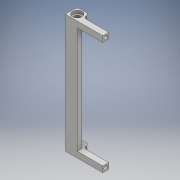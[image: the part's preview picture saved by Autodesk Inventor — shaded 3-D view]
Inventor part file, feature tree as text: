
AUTODESK INVENTOR PART (.ipt)
format: ipt  version: 2018 (Build 220112000, 112)  size: 217,088 bytes
history: native  units: mm
features: extrude x11, sketch x11, fillet x3
ambient origin geometry x8: Origin, YZ Plane, XZ Plane, XY Plane, X Axis, Y Axis, Z Axis, Center Point
bodies: Solid1 (feature_tree)
feature tree (25):
  extrude  "Extrusion1"  Depth=200.0mm
  extrude  "Extrusion2"  Depth=10.0mm
  extrude  "Extrusion3"  Depth=60.0mm TaperAngle=0.0deg
  extrude  "Extrusion4"  Depth=20.0mm
  fillet  "Fillet1"  Radius=30.0mm
  fillet  "Fillet2"  Radius=20.0mm
  extrude  "Extrusion5"  Depth=16.0mm
  extrude  "Extrusion6"  Depth=5.0mm
  extrude  "Extrusion7"  Depth=200.0mm TaperAngle=0.0deg
  fillet  "Fillet3"  Radius=10.0mm
  extrude  "Extrusion8"  Depth=20.0mm
  extrude  "Extrusion9"  Depth=16.0mm
  sketch  "Sketch10"  dims[d27=10.0mm d28=0.0mm d29=5.0mm]
  extrude  "Extrusion10"  Depth=5.0mm
  extrude  "Extrusion11"  Depth=20.0mm
  sketch  "Sketch1"  dims[d0=10.0mm d1=200.0mm]
  sketch  "Sketch2"  dims[d2=3.0mm d3=0.0mm d4=10.0mm]
  sketch  "Sketch3"  dims[d5=10.0mm d6=60.0mm d7=0.0mm]
  sketch  "Sketch4"  dims[d8=6.35mm d9=6.35mm d10=30.0mm d11=0.0mm d12=20.0mm]
  sketch  "Sketch5"  dims[d13=20.0mm d14=16.0mm]
  sketch  "Sketch6"  dims[d15=10.0mm d16=0.0mm d17=5.0mm]
  sketch  "Sketch7"  dims[d18=5.0mm d19=200.0mm d20=0.0mm d21=10.0mm]
  sketch  "Sketch8"  dims[d22=5.0mm d23=0.0mm d24=20.0mm]
  sketch  "Sketch9"  dims[d25=20.0mm d26=16.0mm]
  sketch  "Sketch11"  dims[d30=5.0mm d31=0.0mm d32=20.0mm d33=2.0mm d34=190.0mm d35=0.0mm d36=3.0mm d37=10.0mm d38=0.0mm d39=6.0mm d40=0.0mm]
